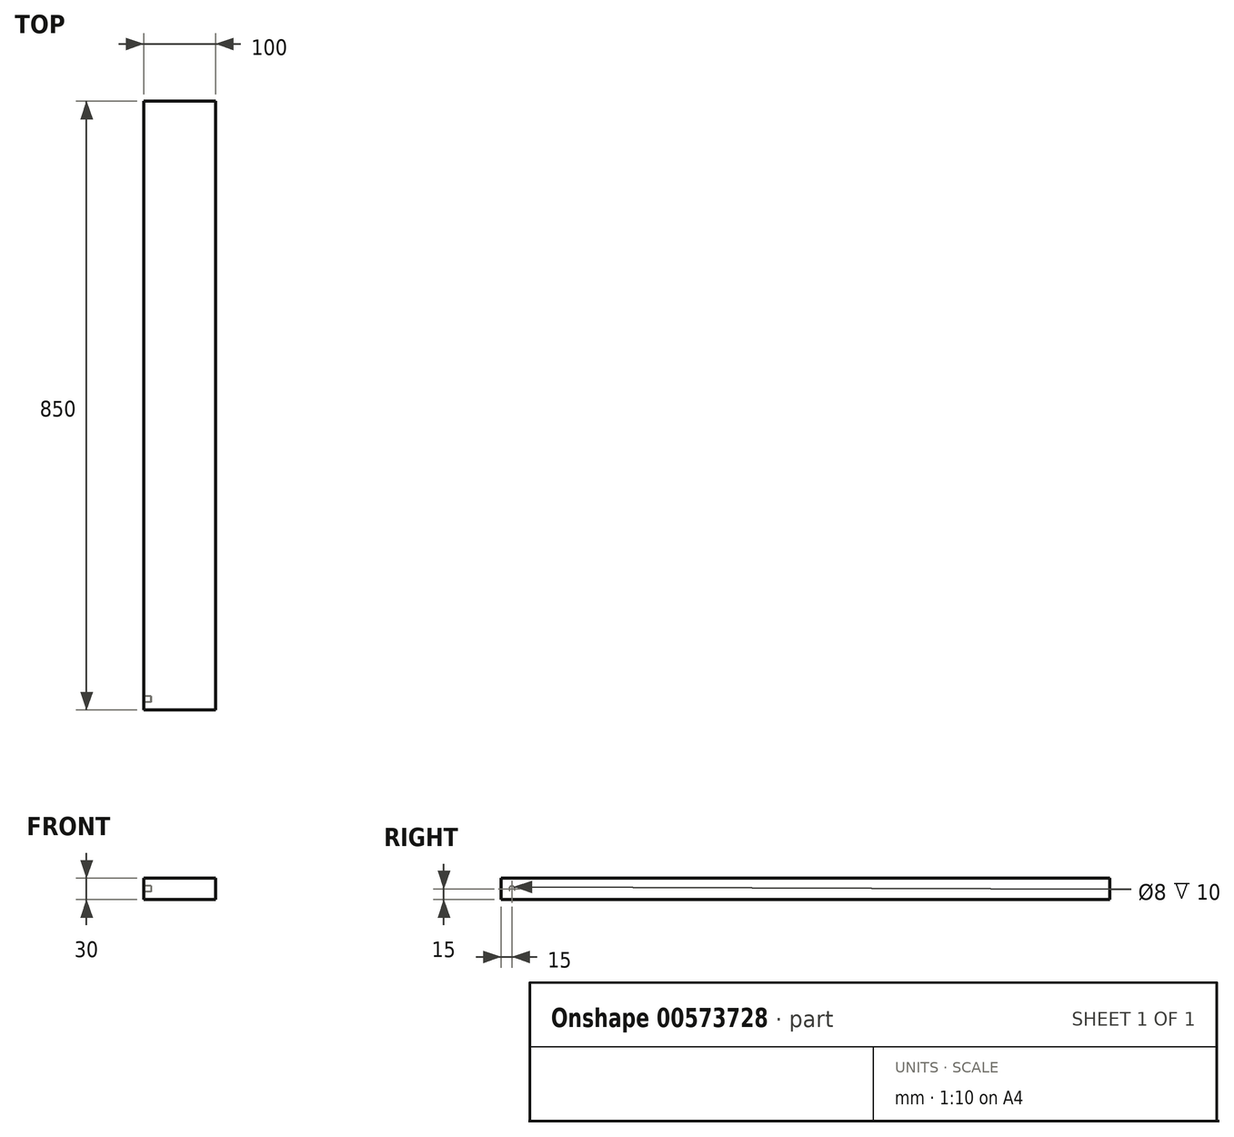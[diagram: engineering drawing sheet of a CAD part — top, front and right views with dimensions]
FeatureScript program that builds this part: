
annotation { "Feature Type Name" : "Feature", "Feature Type Description" : "" }
export const myFeature = defineFeature(function(context is Context, id is Id, definition is map)
    precondition{}
    {
        {
            var Q0;
            Q0=qCreatedBy(makeId("Top.planeOp"),FACE);
            var sketch = newSketch(context, id + "F0", { "sketchPlane" : qUnion([Q0])});
            skLineSegment(sketch, "E0.bottom", {"start": v(0, 0) * mm, "end": v(100, 0) * mm});
            skLineSegment(sketch, "E0.top", {"start": v(0, 850) * mm, "end": v(100, 850) * mm});
            skLineSegment(sketch, "E0.left", {"start": v(0, 0) * mm, "end": v(0, 850) * mm});
            skLineSegment(sketch, "E0.right", {"start": v(100, 0) * mm, "end": v(100, 850) * mm});
            skSolve(sketch);
        }
        {
            var Q0;
            Q0=makeQuery(id+"F0.imprint","IMPRINT",FACE,{"disambiguationData":[TD([[makeQuery(id+"F0.imprint","IMPRINT",EDGE,{"derivedFrom":sQuery(id+"F0.wireOp",EDGE,"E0.bottom")}),1.0]])]});
            extrude(context, id + "F1", {"entities" : qUnion([Q0]), "depth" : 30 * mm, "offsetDistance" : 25 * mm});
        }
        {
            var Q0;
            Q0=makeQuery(id+"F1.opExtrude","SWEPT_FACE",FACE,{"disambiguationData":[OSD([sQuery(id+"F0.wireOp",EDGE,"E0.left")])]});
            var sketch = newSketch(context, id + "F2", { "sketchPlane" : qUnion([Q0])});
            skCircle(sketch, "E1", {"center": v(-15, 15) * mm, "radius": 4 * mm});
            skSolve(sketch);
        }
        {
            var Q0;
            Q0 = qSketchRegion(id + "F2", true);
            extrude(context, id + "F3", {"entities" : qUnion([Q0]), "operationType" : NewBodyOperationType.REMOVE, "oppositeDirection" : true, "depth" : 10 * mm, "offsetDistance" : 25 * mm});
        }
    });
